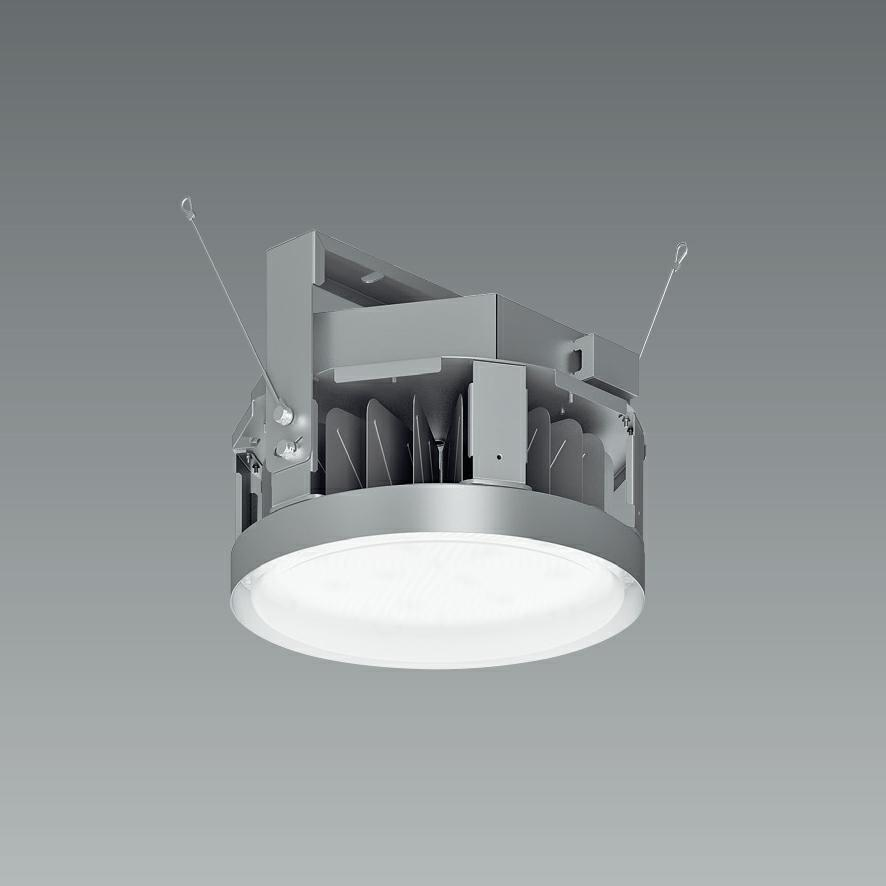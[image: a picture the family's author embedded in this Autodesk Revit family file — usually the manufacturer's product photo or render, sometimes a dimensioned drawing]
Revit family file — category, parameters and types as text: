
# Revit family: EFG5550S
name_source: partatom
category: 照明器具
units: mm (PartAtom-declared; Revit-internal decimal feet)

## family parameters
OmniClass タイトル = Downlights
OmniClass 番号 = 23.80.70.11.14.11
パーツ タイプ = 標準
ロード時にボイドで切り取り = はい
丸型コネクタ寸法 = 直径を使用
作業面ベース = いいえ
光源 = はい
共有 = いいえ
常に垂直 = いいえ
注釈の向きを維持 = いいえ
部屋計算ポイント = はい

## types (1)
- EFG5550S
    BLCJ仕様バージョン = 2
    Clearance Back = 0  [stored 0 ft]
    Clearance Bottom = 0  [stored 0 ft]
    Clearance Front = 0  [stored 0 ft]
    Clearance Left = 0  [stored 0 ft]
    Clearance Right = 0  [stored 0 ft]
    Clearance Top = 0  [stored 0 ft]
    Depth = 0  [stored 0 ft]
    FamilyVersion = v2.0
    Height = 290  [stored 0.951444 ft]
    IfcExportAs = IfcLightFixtureType
    IfcExportType = DIRECTIONSOURCE
    OmniClassCode = 23.80.70.11.14.11
    URL = https://data2.endo-lighting.co.jp
    Width = 0  [stored 0 ft]
    イメージ(タイプ) = EFG5550S-K.jpg
    カラー フィルタ = 16777215
    サービススペース表示 = いいえ
    シンボル表示 = はい
    データ作成年月 = 2025.03
    フォトメトリック Web ファイル = EFG5550S.IES
    モデル = EFG5550S
    ランプ = LED
    ランプ_全光束 = 0 lm
    ランプ_定格消費効率(lm/W) = 0
    ランプ_定格消費電力 = 0 W
    ランプ_本数 = 0
    ランプ_電流 = 0 A
    ランプの種類 = LED
    価格 = 191000 $
    傾斜角 = -90.00°
    公共型番 = LSR1W-200
    分類グループ = 電気
    分類コード = 40305100000000
    周波数 = 0 Hz
    呼称 = 高天井
    固有エネルギー消費効率(lm/W) = 146.8
    埋込深さ = 0
    埋込穴寸法 = 0
    安定器_二次電圧 = 0 V
    安定器_入力電力 = 0 W
    安定器_入力電流 = 0 A
    安定器_定格電圧 = 0 V
    定格光束 = 20118 lm
    定格入力容量 = 141 VA
    定格入力電圧 = 200 V
    定格入力電流 = 0 A
    定格消費電力 = 137 W
    平均演色評価数(Ra) = 82
    既定の高さ = 0  [stored 0 ft]
    材質_カバー = <カテゴリ別>
    材質_ルーバー = <カテゴリ別>
    材質_反射板 = <カテゴリ別>
    材質_本体 = <カテゴリ別>
    極数 = 1
    用途 = E_一般照明
    皮相負荷 = 141 VA
    直径 = 428  [stored 1.4042 ft]
    相 = 1
    積算_科目 = 1 電灯設備
    積算_科目2 = [1_1]照明
    製品リリース年月 = 2024.04
    製品質量 = 6.70 kg
    製造元 = 株式会社遠藤照明
    説明 = 防眩・小型シーリングライト
    調光ランプの色温度変化。 = <なし>
    負荷分類 = 8_照明
    質量 = 0.00 kg
    運転質量 = 0.00 kg
    配光角 = 0
    電源種別_記号 = AC

note: [stored X ft] marks values corroborated as IEEE doubles in the binary element streams (Revit-internal decimal feet)
